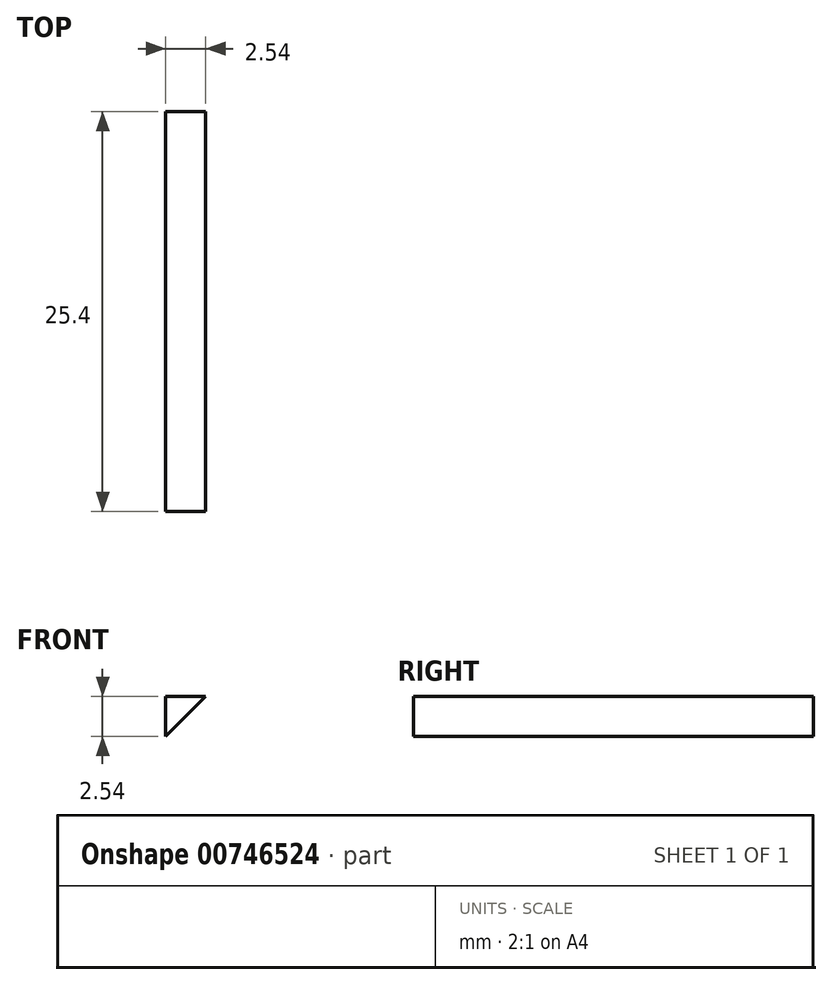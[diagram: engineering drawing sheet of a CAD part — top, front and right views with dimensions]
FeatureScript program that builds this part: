
annotation { "Feature Type Name" : "Feature", "Feature Type Description" : "" }
export const myFeature = defineFeature(function(context is Context, id is Id, definition is map)
    precondition{}
    {
        {
            var Q0;
            Q0=qCreatedBy(makeId("Front.planeOp"),FACE);
            var sketch = newSketch(context, id + "F0", { "sketchPlane" : qUnion([Q0])});
            skLineSegment(sketch, "E0", {"start": v(-9.7, 7.14) * mm, "end": v(-9.7, 9.68) * mm});
            skLineSegment(sketch, "E1", {"start": v(-9.7, 9.68) * mm, "end": v(-7.15, 9.68) * mm});
            skLineSegment(sketch, "E2", {"start": v(-7.15, 9.68) * mm, "end": v(-9.7, 7.14) * mm});
            skSolve(sketch);
        }
        {
            var Q0;
            Q0=makeQuery(id+"F0.imprint","IMPRINT",FACE,{"disambiguationData":[TD([[makeQuery(id+"F0.imprint","IMPRINT",EDGE,{"derivedFrom":sQuery(id+"F0.wireOp",EDGE,"E0")}),-1.0]])]});
            extrude(context, id + "F1", {"entities" : qUnion([Q0]), "depth" : 25.4 * mm, "offsetDistance" : 25.4 * mm});
        }
    });
